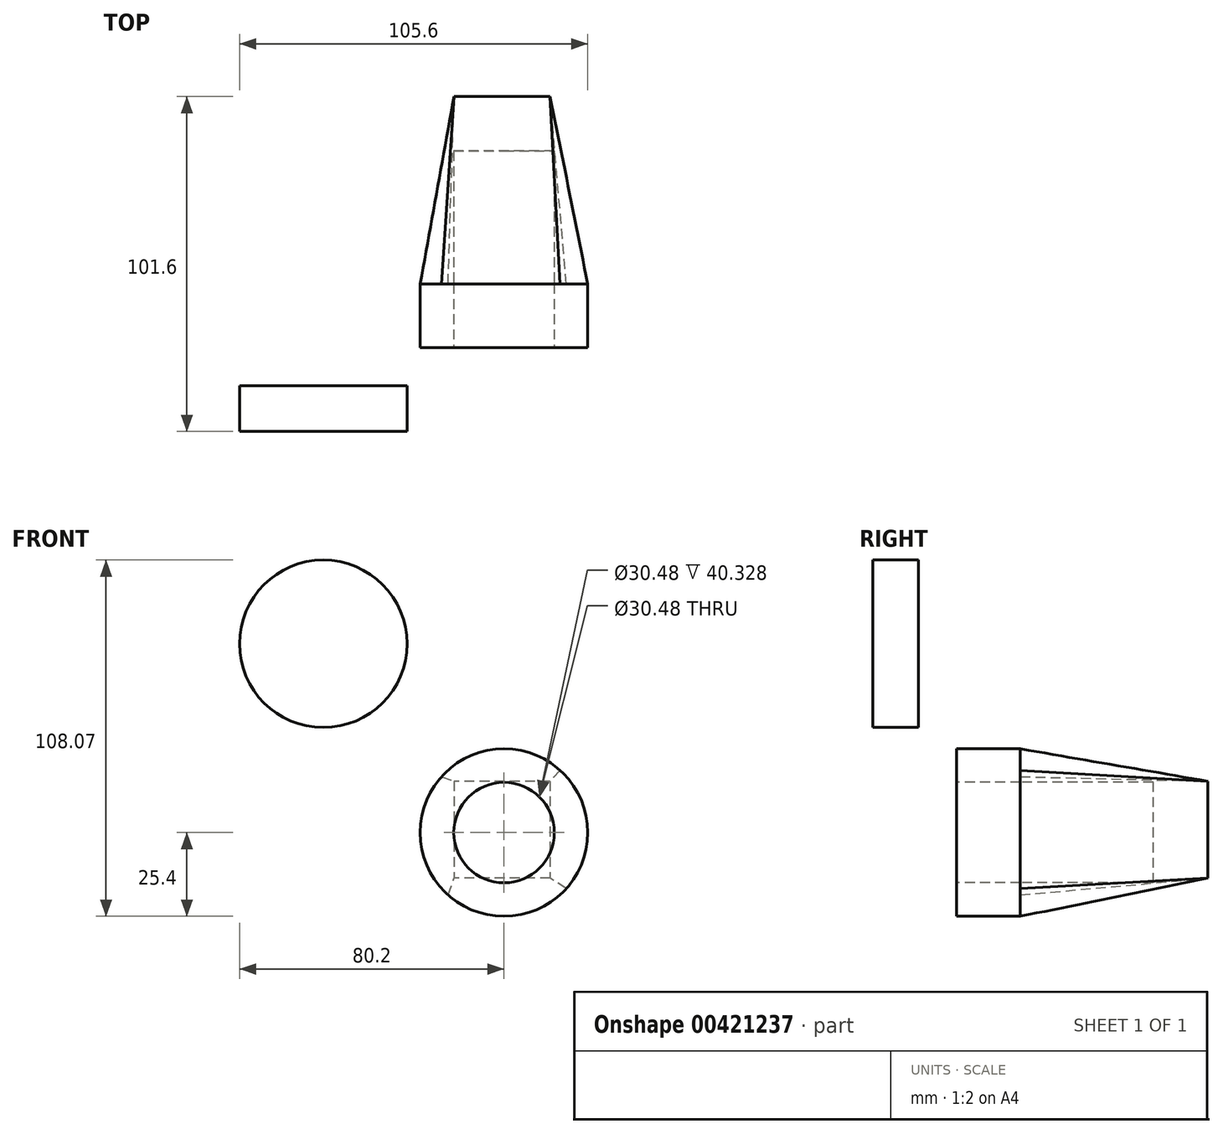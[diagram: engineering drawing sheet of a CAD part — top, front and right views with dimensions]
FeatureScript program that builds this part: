
annotation { "Feature Type Name" : "Feature", "Feature Type Description" : "" }
export const myFeature = defineFeature(function(context is Context, id is Id, definition is map)
    precondition{}
    {
        {
            var Q0;
            Q0=qCreatedBy(makeId("Front.planeOp"),FACE);
            var sketch = newSketch(context, id + "F0", { "sketchPlane" : qUnion([Q0])});
            skCircle(sketch, "E0", {"center": v(0, 0) * mm, "radius": 25.4 * mm});
            skSolve(sketch);
        }
        {
            var Q0;
            Q0=makeQuery(id+"F0.imprint","IMPRINT",FACE,{"disambiguationData":[TD([[makeQuery(id+"F0.imprint","IMPRINT",EDGE,{"derivedFrom":sQuery(id+"F0.wireOp",EDGE,"E0")}),1.0]])]});
            extrude(context, id + "F1", {"entities" : qUnion([Q0]), "depth" : 76.2 * mm});
        }
        {
            var Q0;
            Q0=qCreatedBy(makeId("Right.planeOp"),FACE);
            var sketch = newSketch(context, id + "F2", { "sketchPlane" : qUnion([Q0])});
            skLineSegment(sketch, "E1.bottom", {"start": v(-56.84, 29) * mm, "end": v(2.91, 29) * mm});
            skLineSegment(sketch, "E1.top", {"start": v(-56.84, -29.58) * mm, "end": v(2.91, -29.58) * mm});
            skLineSegment(sketch, "E1.left", {"start": v(-56.84, 29) * mm, "end": v(-56.84, -29.58) * mm});
            skLineSegment(sketch, "E1.right", {"start": v(2.91, 29) * mm, "end": v(2.91, -29.58) * mm});
            skSolve(sketch);
        }
        {
            var Q0;
            Q0=makeQuery(id+"F2.imprint","IMPRINT",FACE,{"disambiguationData":[TD([[makeQuery(id+"F2.imprint","IMPRINT",EDGE,{"derivedFrom":sQuery(id+"F2.wireOp",EDGE,"E1.bottom")}),-1.0]])]});
            extrude(context, id + "F3", {"entities" : qUnion([Q0]), "operationType" : NewBodyOperationType.REMOVE, "oppositeDirection" : true, "depth" : 43.43 * mm, "hasSecondDirection" : true, "secondDirectionOppositeDirection" : false, "secondDirectionDepth" : 30.23 * mm});
        }
        {
            var Q0;
            Q0=qCreatedBy(makeId("Front.planeOp"),FACE);
            var sketch = newSketch(context, id + "F4", { "sketchPlane" : qUnion([Q0])});
            skLineSegment(sketch, "E2.bottom", {"start": v(14, 15.6) * mm, "end": v(-15.16, 15.6) * mm});
            skLineSegment(sketch, "E2.top", {"start": v(14, -13.85) * mm, "end": v(-15.16, -13.85) * mm});
            skLineSegment(sketch, "E2.left", {"start": v(14, 15.6) * mm, "end": v(14, -13.85) * mm});
            skLineSegment(sketch, "E2.right", {"start": v(-15.16, 15.6) * mm, "end": v(-15.16, -13.85) * mm});
            skSolve(sketch);
        }
        {
            var Q0;
            Q0=makeQuery(id+"F3.boolean.opBoolean","COPY",FACE,{"derivedFrom":makeQuery(id+"F3.opExtrude","SWEPT_FACE",FACE,{"disambiguationData":[OSD([sQuery(id+"F2.wireOp",EDGE,"E1.left")])]})});
            var Q1;
            Q1=makeQuery(id+"F4.imprint","IMPRINT",FACE,{"disambiguationData":[TD([[makeQuery(id+"F4.imprint","IMPRINT",EDGE,{"derivedFrom":sQuery(id+"F4.wireOp",EDGE,"E2.bottom")}),1.0]])]});
            loft(context, id + "F5", {"sheetProfilesArray" : [{ "sheetProfileEntities" : qUnion([Q0]) }, { "sheetProfileEntities" : qUnion([Q1]) }]});
        }
        {
            var Q0;
            Q0=makeQuery(id+"F1.opExtrude","CAP_FACE",FACE,{"disambiguationData":[OSD([sQuery(id+"F0.wireOp",EDGE,"E0")])],"isStart":false});
            var sketch = newSketch(context, id + "F6", { "sketchPlane" : qUnion([Q0])});
            skCircle(sketch, "E3", {"center": v(0, 0) * mm, "radius": 15.24 * mm});
            skSolve(sketch);
        }
        {
            var Q0;
            Q0=makeQuery(id+"F6.imprint","IMPRINT",FACE,{"disambiguationData":[TD([[makeQuery(id+"F6.imprint","IMPRINT",EDGE,{"derivedFrom":sQuery(id+"F6.wireOp",EDGE,"E3")}),1.0]])]});
            extrude(context, id + "F7", {"entities" : qUnion([Q0]), "operationType" : NewBodyOperationType.REMOVE, "oppositeDirection" : true, "depth" : 59.69 * mm});
        }
        {
            var Q0;
            Q0=qCreatedBy(makeId("Front.planeOp"),FACE);
            var sketch = newSketch(context, id + "F8", { "sketchPlane" : qUnion([Q0])});
            skCircle(sketch, "E4", {"center": v(-54.8, 57.27) * mm, "radius": 25.4 * mm});
            skSolve(sketch);
        }
        {
            var Q0;
            Q0=makeQuery(id+"F8.imprint","IMPRINT",FACE,{"disambiguationData":[TD([[makeQuery(id+"F8.imprint","IMPRINT",EDGE,{"derivedFrom":sQuery(id+"F8.wireOp",EDGE,"E4")}),1.0]])]});
            extrude(context, id + "F9", {"entities" : qUnion([Q0]), "depth" : 101.6 * mm});
        }
        {
            var Q0;
            Q0=qCreatedBy(makeId("Right.planeOp"),FACE);
            var sketch = newSketch(context, id + "F10", { "sketchPlane" : qUnion([Q0])});
            skLineSegment(sketch, "E5.bottom", {"start": v(-87.72, 84.04) * mm, "end": v(5.76, 84.04) * mm});
            skLineSegment(sketch, "E5.top", {"start": v(-87.72, 28.83) * mm, "end": v(5.76, 28.83) * mm});
            skLineSegment(sketch, "E5.left", {"start": v(-87.72, 84.04) * mm, "end": v(-87.72, 28.83) * mm});
            skLineSegment(sketch, "E5.right", {"start": v(5.76, 84.04) * mm, "end": v(5.76, 28.83) * mm});
            skSolve(sketch);
        }
        {
            var Q0;
            Q0 = qSketchRegion(id + "F10", true);
            extrude(context, id + "F11", {"entities" : qUnion([Q0]), "operationType" : NewBodyOperationType.REMOVE, "oppositeDirection" : true, "depth" : 89.92 * mm});
        }
    });
